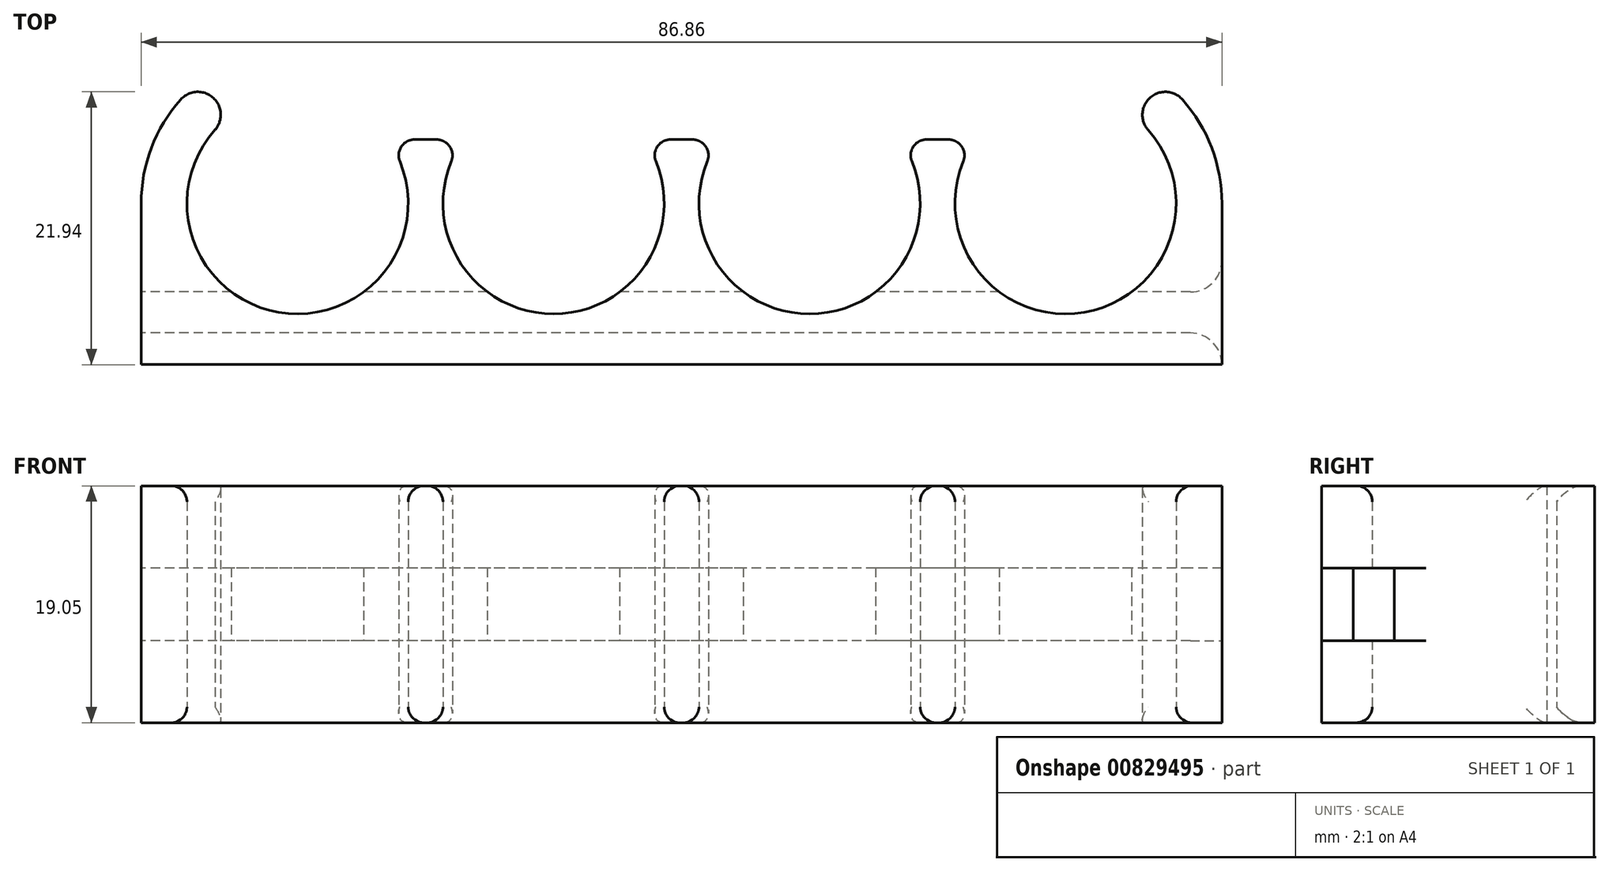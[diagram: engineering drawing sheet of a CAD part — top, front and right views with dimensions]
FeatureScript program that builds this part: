
annotation { "Feature Type Name" : "Feature", "Feature Type Description" : "" }
export const myFeature = defineFeature(function(context is Context, id is Id, definition is map)
    precondition{}
    {
        {
            var Q0;
            Q0=qCreatedBy(makeId("Top.planeOp"),FACE);
            var sketch = newSketch(context, id + "F0", { "sketchPlane" : qUnion([Q0])});
            skLineSegment(sketch, "E0.direction1", {"start": v(0, 0) * mm, "end": v(20.57, 0) * mm, "construction": true});
            skLineSegment(sketch, "E1", {"start": v(9.4, 5.14) * mm, "end": v(11.18, 5.14) * mm});
            skLineSegment(sketch, "E2", {"start": v(29.97, 5.14) * mm, "end": v(31.75, 5.14) * mm});
            skArc(sketch, "E3.MirrorCS", {"start": v(-9.4, 8.35) * mm, "mid": v(-6.78, 8.5) * mm, "end": v(-6.66, 5.9) * mm});
            skArc(sketch, "E4.MirrorCS", {"start": v(-12.57, 0) * mm, "mid": v(-11.75, 4.47) * mm, "end": v(-9.4, 8.35) * mm});
            skLineSegment(sketch, "E5.MirrorCS", {"start": v(-12.57, -12.97) * mm, "end": v(-12.57, 0) * mm});
            skArc(sketch, "E6", {"start": v(8.22, 3.38) * mm, "mid": v(-1.5, -8.76) * mm, "end": v(-6.63, 5.93) * mm});
            skArc(sketch, "E7", {"start": v(28.8, 3.38) * mm, "mid": v(20.57, -8.89) * mm, "end": v(12.35, 3.38) * mm});
            skPoint(sketch, "E8.visualSharp", {"position": v(7.26, 5.14) * mm});
            skArc(sketch, "E8.filletArc", {"start": v(9.4, 5.14) * mm, "mid": v(8.34, 4.57) * mm, "end": v(8.22, 3.38) * mm});
            skPoint(sketch, "E9.visualSharp", {"position": v(13.32, 5.14) * mm});
            skArc(sketch, "E9.filletArc", {"start": v(12.35, 3.38) * mm, "mid": v(12.23, 4.57) * mm, "end": v(11.18, 5.14) * mm});
            skPoint(sketch, "E10.visualSharp", {"position": v(27.83, 5.14) * mm});
            skArc(sketch, "E10.filletArc", {"start": v(29.97, 5.14) * mm, "mid": v(28.91, 4.57) * mm, "end": v(28.8, 3.38) * mm});
            skPoint(sketch, "E11.visualSharp", {"position": v(33.9, 5.14) * mm});
            skArc(sketch, "E11.filletArc", {"start": v(32.93, 3.38) * mm, "mid": v(32.8, 4.57) * mm, "end": v(31.75, 5.14) * mm});
            skLineSegment(sketch, "E12", {"start": v(74.3, -12.97) * mm, "end": v(74.3, 0) * mm});
            skLineSegment(sketch, "E13", {"start": v(50.54, 5.14) * mm, "end": v(52.33, 5.14) * mm});
            skArc(sketch, "E14", {"start": v(74.3, 0) * mm, "mid": v(73.47, 4.47) * mm, "end": v(71.11, 8.35) * mm});
            skArc(sketch, "E15", {"start": v(71.11, 8.35) * mm, "mid": v(68.52, 8.5) * mm, "end": v(68.36, 5.9) * mm});
            skArc(sketch, "E16", {"start": v(49.37, 3.38) * mm, "mid": v(41.15, -8.9) * mm, "end": v(32.93, 3.38) * mm});
            skArc(sketch, "E17", {"start": v(68.36, 5.9) * mm, "mid": v(63.21, -8.76) * mm, "end": v(53.5, 3.38) * mm});
            skPoint(sketch, "E18.visualSharp", {"position": v(48.4, 5.14) * mm});
            skArc(sketch, "E18.filletArc", {"start": v(50.54, 5.14) * mm, "mid": v(49.49, 4.57) * mm, "end": v(49.37, 3.38) * mm});
            skPoint(sketch, "E19.visualSharp", {"position": v(54.47, 5.14) * mm});
            skArc(sketch, "E19.filletArc", {"start": v(53.5, 3.38) * mm, "mid": v(53.38, 4.57) * mm, "end": v(52.33, 5.14) * mm});
            skLineSegment(sketch, "E20", {"start": v(-12.57, -12.97) * mm, "end": v(74.3, -12.97) * mm});
            skSolve(sketch);
        }
        {
            var Q0;
            Q0=makeQuery(id+"F0.imprint","IMPRINT",FACE,{"disambiguationData":[TD([[makeQuery(id+"F0.imprint","IMPRINT",EDGE,{"derivedFrom":sQuery(id+"F0.wireOp",EDGE,"E1")}),-1.0]])]});
            var Q1;
            Q1=sQuery(id+"F0.wireOp",EDGE,"E20");
            var Q2;
            Q2=sQuery(id+"F0.wireOp",EDGE,"E6");
            var Q3;
            Q3=sQuery(id+"F0.wireOp",EDGE,"E3.MirrorCS");
            var Q4;
            Q4=sQuery(id+"F0.wireOp",EDGE,"E4.MirrorCS");
            var Q5;
            Q5=sQuery(id+"F0.wireOp",EDGE,"E5.MirrorCS");
            var Q6;
            Q6=sQuery(id+"F0.wireOp",EDGE,"E7");
            var Q7;
            Q7=sQuery(id+"F0.wireOp",EDGE,"E16");
            var Q8;
            Q8=sQuery(id+"F0.wireOp",EDGE,"E17");
            var Q9;
            Q9=sQuery(id+"F0.wireOp",EDGE,"E12");
            var Q10;
            Q10=sQuery(id+"F0.wireOp",EDGE,"E14");
            var Q11;
            Q11=sQuery(id+"F0.wireOp",EDGE,"E15");
            var Q12;
            Q12=sQuery(id+"F0.wireOp",EDGE,"E19.filletArc");
            var Q13;
            Q13=sQuery(id+"F0.wireOp",EDGE,"E13");
            var Q14;
            Q14=sQuery(id+"F0.wireOp",EDGE,"E18.filletArc");
            var Q15;
            Q15=sQuery(id+"F0.wireOp",EDGE,"E11.filletArc");
            var Q16;
            Q16=sQuery(id+"F0.wireOp",EDGE,"E2");
            var Q17;
            Q17=sQuery(id+"F0.wireOp",EDGE,"E10.filletArc");
            var Q18;
            Q18=sQuery(id+"F0.wireOp",EDGE,"E9.filletArc");
            var Q19;
            Q19=sQuery(id+"F0.wireOp",EDGE,"E1");
            var Q20;
            Q20=sQuery(id+"F0.wireOp",EDGE,"E8.filletArc");
            extrude(context, id + "F1", {"entities" : qUnion([Q0]), "surfaceEntities" : qUnion([Q1, Q2, Q3, Q4, Q5, Q6, Q7, Q8, Q9, Q10, Q11, Q12, Q13, Q14, Q15, Q16, Q17, Q18, Q19, Q20]), "depth" : 19.05 * mm, "offsetDistance" : 25.4 * mm});
        }
        {
            var Q0;
            Q0=makeQuery(id+"F1.opExtrude","SWEPT_FACE",FACE,{"disambiguationData":[OSD([sQuery(id+"F0.wireOp",EDGE,"E5.MirrorCS")])]});
            cPlane(context, id + "F2", {"entities" : qUnion([Q0]), "cplaneType" : CPlaneType.OFFSET, "offset" : 0 * mm, "width" : 152.4 * mm, "height" : 152.4 * mm});
        }
        {
            var Q0;
            Q0=qCreatedBy(id+"F2.planeOp",FACE);
            var sketch = newSketch(context, id + "F3", { "sketchPlane" : qUnion([Q0])});
            skLineSegment(sketch, "E21.bottom", {"start": v(7.13, 12.45) * mm, "end": v(10.43, 12.45) * mm});
            skLineSegment(sketch, "E21.top", {"start": v(7.13, 6.6) * mm, "end": v(10.43, 6.6) * mm});
            skLineSegment(sketch, "E21.left", {"start": v(7.13, 12.45) * mm, "end": v(7.13, 6.6) * mm});
            skLineSegment(sketch, "E21.right", {"start": v(10.43, 12.45) * mm, "end": v(10.43, 6.6) * mm});
            skLineSegment(sketch, "E22", {"start": v(10.43, 9.53) * mm, "end": v(7.13, 9.53) * mm, "construction": true});
            skLineSegment(sketch, "E23", {"start": v(12.97, 9.53) * mm, "end": v(7.13, 9.53) * mm, "construction": true});
            skSolve(sketch);
        }
        {
            var Q0;
            Q0=makeQuery(id+"F3.imprint","IMPRINT",FACE,{"disambiguationData":[TD([[makeQuery(id+"F3.imprint","IMPRINT",EDGE,{"derivedFrom":sQuery(id+"F3.wireOp",EDGE,"E21.bottom")}),-1.0]])]});
            extrude(context, id + "F4", {"entities" : qUnion([Q0]), "operationType" : NewBodyOperationType.REMOVE, "endBound" : BoundingType.THROUGH_ALL, "oppositeDirection" : true, "depth" : 25.4 * mm, "offsetDistance" : 25.4 * mm});
        }
        {
            var Q0;
            Q0=makeQuery(id+"F4.boolean.opBoolean","INTERSECT",EDGE,{"derivedFrom":[makeQuery(id+"F1.opExtrude","SWEPT_FACE",FACE,{"disambiguationData":[OSD([sQuery(id+"F0.wireOp",EDGE,"E12")])]}),makeQuery(id+"F4.opExtrude","SWEPT_FACE",FACE,{"disambiguationData":[OSD([sQuery(id+"F3.wireOp",EDGE,"E21.left")])]})]});
            var Q1;
            Q1=makeQuery(id+"F4.boolean.opBoolean","COPY",EDGE,{"derivedFrom":makeQuery(id+"F4.opExtrude","CAP_EDGE",EDGE,{"disambiguationData":[OSD([sQuery(id+"F3.wireOp",EDGE,"E21.left")])],"isStart":true})});
            var Q2;
            Q2=makeQuery(id+"F4.boolean.opBoolean","COPY",EDGE,{"derivedFrom":makeQuery(id+"F4.opExtrude","CAP_EDGE",EDGE,{"disambiguationData":[OSD([sQuery(id+"F3.wireOp",EDGE,"E21.right")])],"isStart":true})});
            var Q3;
            Q3=makeQuery(id+"F4.boolean.opBoolean","INTERSECT",EDGE,{"derivedFrom":[makeQuery(id+"F1.opExtrude","SWEPT_FACE",FACE,{"disambiguationData":[OSD([sQuery(id+"F0.wireOp",EDGE,"E12")])]}),makeQuery(id+"F4.opExtrude","SWEPT_FACE",FACE,{"disambiguationData":[OSD([sQuery(id+"F3.wireOp",EDGE,"E21.right")])]})]});
            fillet(context, id + "F5", {"entities" : qUnion([Q0, Q1, Q2, Q3]), "radius" : 2.54 * mm, "tangentPropagation" : true, "allowEdgeOverflow" : false});
        }
        {
            var Q0;
            Q0=makeQuery(id+"F1.opExtrude","CAP_EDGE",EDGE,{"disambiguationData":[OSD([sQuery(id+"F0.wireOp",EDGE,"wjlftGJZ-UNCk-L4i5-wpio-xcS1ndEBSDBN")])],"isStart":true});
            var Q1;
            Q1=makeQuery(id+"F1.opExtrude","CAP_EDGE",EDGE,{"disambiguationData":[OSD([sQuery(id+"F0.wireOp",EDGE,"E7")])],"isStart":true});
            var Q2;
            Q2=makeQuery(id+"F1.opExtrude","CAP_EDGE",EDGE,{"disambiguationData":[OSD([sQuery(id+"F0.wireOp",EDGE,"E6")])],"isStart":true});
            var Q3;
            Q3=makeQuery(id+"F1.opExtrude","CAP_EDGE",EDGE,{"disambiguationData":[OSD([sQuery(id+"F0.wireOp",EDGE,"E17")])],"isStart":true});
            var Q4;
            Q4=makeQuery(id+"F1.opExtrude","CAP_EDGE",EDGE,{"disambiguationData":[OSD([sQuery(id+"F0.wireOp",EDGE,"E16")])],"isStart":true});
            var Q5;
            Q5=makeQuery(id+"F1.opExtrude","CAP_EDGE",EDGE,{"disambiguationData":[OSD([sQuery(id+"F0.wireOp",EDGE,"E17")])],"isStart":false});
            var Q6;
            Q6=makeQuery(id+"F1.opExtrude","CAP_EDGE",EDGE,{"disambiguationData":[OSD([sQuery(id+"F0.wireOp",EDGE,"E16")])],"isStart":false});
            var Q7;
            Q7=makeQuery(id+"F1.opExtrude","CAP_EDGE",EDGE,{"disambiguationData":[OSD([sQuery(id+"F0.wireOp",EDGE,"E7")])],"isStart":false});
            var Q8;
            Q8=makeQuery(id+"F1.opExtrude","CAP_EDGE",EDGE,{"disambiguationData":[OSD([sQuery(id+"F0.wireOp",EDGE,"E6")])],"isStart":false});
            fillet(context, id + "F6", {"entities" : qUnion([Q0, Q1, Q2, Q3, Q4, Q5, Q6, Q7, Q8]), "radius" : 1.27 * mm, "allowEdgeOverflow" : false});
        }
    });
